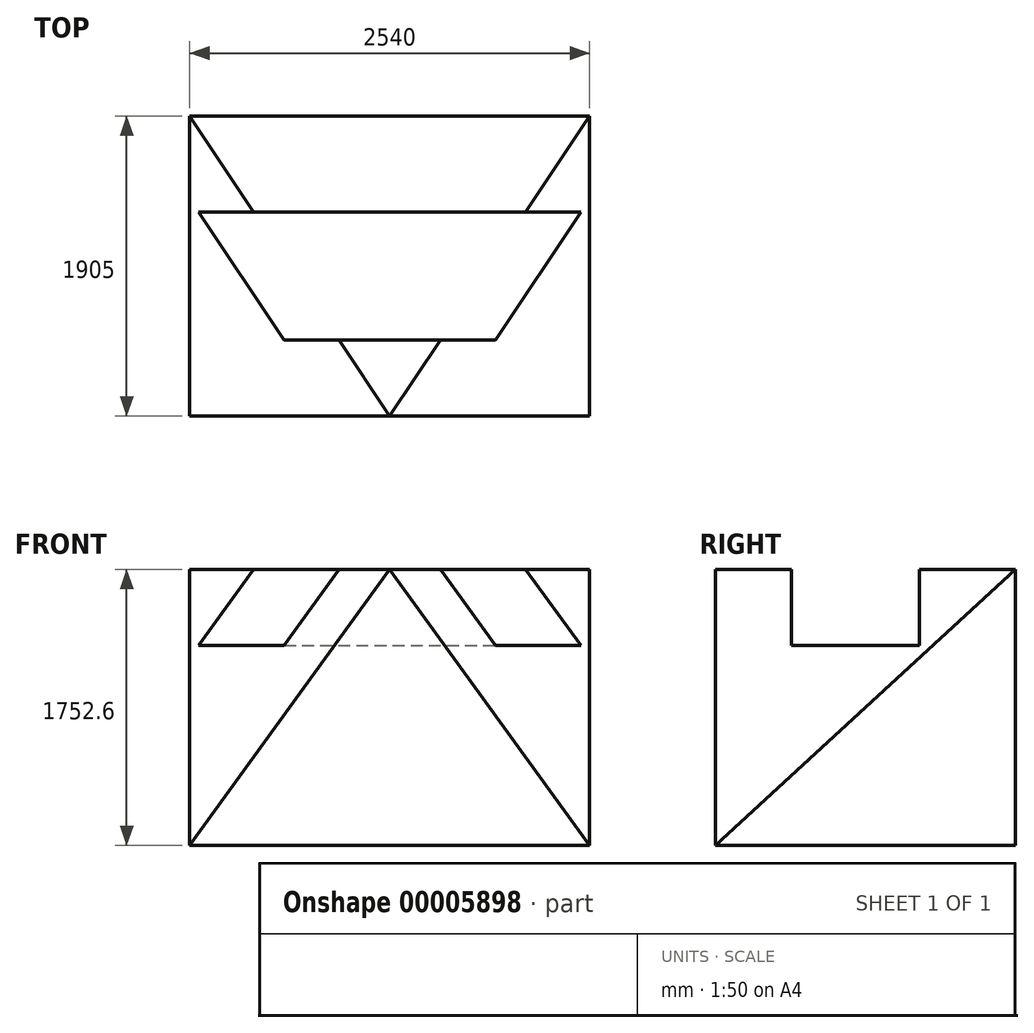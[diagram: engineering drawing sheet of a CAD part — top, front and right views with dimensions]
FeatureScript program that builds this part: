
annotation { "Feature Type Name" : "Feature", "Feature Type Description" : "" }
export const myFeature = defineFeature(function(context is Context, id is Id, definition is map)
    precondition{}
    {
        {
            var Q0;
            Q0=qCreatedBy(makeId("Front.planeOp"),FACE);
            var sketch = newSketch(context, id + "F0", { "sketchPlane" : qUnion([Q0])});
            skLineSegment(sketch, "E0", {"start": v(0, 0) * mm, "end": v(2540, 0) * mm});
            skLineSegment(sketch, "E1", {"start": v(2540, 0) * mm, "end": v(2540, -1752.6) * mm});
            skLineSegment(sketch, "E2", {"start": v(2540, -1752.6) * mm, "end": v(0, -1752.6) * mm});
            skLineSegment(sketch, "E3", {"start": v(0, -1752.6) * mm, "end": v(0, 0) * mm});
            skSolve(sketch);
        }
        {
            var Q0;
            Q0=makeQuery(id+"F0.imprint","IMPRINT",FACE,{"disambiguationData":[TD([[makeQuery(id+"F0.imprint","IMPRINT",EDGE,{"derivedFrom":sQuery(id+"F0.wireOp",EDGE,"E0")}),-1.0]])]});
            extrude(context, id + "F1", {"entities" : qUnion([Q0]), "depth" : 1905 * mm});
        }
        {
            var Q0;
            Q0=makeQuery(id+"F1.opExtrude","SWEPT_FACE",FACE,{"disambiguationData":[OSD([sQuery(id+"F0.wireOp",EDGE,"E1")])]});
            var sketch = newSketch(context, id + "F2", { "sketchPlane" : qUnion([Q0])});
            skLineSegment(sketch, "E4", {"start": v(0, 0) * mm, "end": v(-1905, -1752.6) * mm});
            skLineSegment(sketch, "E5", {"start": v(-1905, 0) * mm, "end": v(-1422.4, 0) * mm});
            skLineSegment(sketch, "E6", {"start": v(-1422.4, 0) * mm, "end": v(-1422.4, -482.6) * mm});
            skLineSegment(sketch, "E7", {"start": v(-1422.4, -482.6) * mm, "end": v(-609.6, -482.6) * mm});
            skLineSegment(sketch, "E8", {"start": v(-609.6, -482.6) * mm, "end": v(-609.6, 0) * mm});
            skLineSegment(sketch, "E9", {"start": v(-609.6, 0) * mm, "end": v(0, 0) * mm});
            skLineSegment(sketch, "E10", {"start": v(-1905, 0) * mm, "end": v(-1905, -1752.6) * mm});
            skSolve(sketch);
        }
        {
            var Q0;
            Q0=makeQuery(id+"F1.opExtrude","CAP_FACE",FACE,{"disambiguationData":[OSD([sQuery(id+"F0.wireOp",EDGE,"E0"),sQuery(id+"F0.wireOp",EDGE,"E1"),sQuery(id+"F0.wireOp",EDGE,"E2"),sQuery(id+"F0.wireOp",EDGE,"E3")])],"isStart":false});
            var sketch = newSketch(context, id + "F3", { "sketchPlane" : qUnion([Q0])});
            skLineSegment(sketch, "E11", {"start": v(1270, 0) * mm, "end": v(2540, -1752.6) * mm});
            skSolve(sketch);
        }
        {
            var Q0;
            Q0=sQuery(id+"F3.wireOp",VERTEX,"E11.start");
            var Q1;
            Q1=sQuery(id+"F2.wireOp",VERTEX,"E9.end");
            var Q2;
            Q2=sQuery(id+"F3.wireOp",VERTEX,"E11.end");
            cPlane(context, id + "F4", {"entities" : qUnion([Q0, Q1, Q2]), "cplaneType" : CPlaneType.THREE_POINT, "offset" : 152.4 * mm, "width" : 152.4 * mm, "height" : 152.4 * mm});
        }
        {
            var Q0;
            Q0=qCreatedBy(id+"F4.planeOp",FACE);
            var sketch = newSketch(context, id + "F5", { "sketchPlane" : qUnion([Q0])});
            skLineSegment(sketch, "E12", {"start": v(-3737.09, 250.38) * mm, "end": v(-2471.14, -4877.21) * mm});
            skLineSegment(sketch, "E13", {"start": v(-2471.14, -4877.21) * mm, "end": v(9797.3, -2905.45) * mm});
            skLineSegment(sketch, "E14", {"start": v(9797.3, -2905.45) * mm, "end": v(3353.72, 2692.03) * mm});
            skLineSegment(sketch, "E15", {"start": v(3353.72, 2692.03) * mm, "end": v(-3737.09, 250.38) * mm});
            skSolve(sketch);
        }
        {
            var Q0;
            Q0=makeQuery(id+"F5.imprint","IMPRINT",FACE,{"disambiguationData":[TD([[makeQuery(id+"F5.imprint","IMPRINT",EDGE,{"derivedFrom":sQuery(id+"F5.wireOp",EDGE,"E12")}),1.0]])]});
            extrude(context, id + "F6", {"entities" : qUnion([Q0]), "operationType" : NewBodyOperationType.REMOVE, "depth" : 2540 * mm});
        }
        {
            var Q0;
            Q0=makeQuery(id+"F1.opExtrude","CAP_VERTEX",VERTEX,{"disambiguationData":[OSD([sQuery(id+"F0.wireOp",EDGE,"E0"),sQuery(id+"F0.wireOp",EDGE,"E3")])],"isStart":true});
            var Q1;
            Q1=sQuery(id+"F3.wireOp",VERTEX,"E11.start");
            var Q2;
            Q2=makeQuery(id+"F1.opExtrude","CAP_VERTEX",VERTEX,{"disambiguationData":[OSD([sQuery(id+"F0.wireOp",EDGE,"E2"),sQuery(id+"F0.wireOp",EDGE,"E3")])],"isStart":false});
            cPlane(context, id + "F7", {"entities" : qUnion([Q0, Q1, Q2]), "cplaneType" : CPlaneType.THREE_POINT, "offset" : 152.4 * mm, "width" : 152.4 * mm, "height" : 152.4 * mm});
        }
        {
            var Q0;
            Q0=qCreatedBy(id+"F7.planeOp",FACE);
            var sketch = newSketch(context, id + "F8", { "sketchPlane" : qUnion([Q0])});
            skLineSegment(sketch, "E16", {"start": v(-1106.9, 0) * mm, "end": v(6334.9, 2345.3) * mm});
            skLineSegment(sketch, "E17", {"start": v(6334.9, 2345.3) * mm, "end": v(8031.7, -2892.8) * mm});
            skLineSegment(sketch, "E18", {"start": v(8031.7, -2892.8) * mm, "end": v(464.38, -2554.35) * mm});
            skLineSegment(sketch, "E19", {"start": v(464.38, -2554.35) * mm, "end": v(-1106.9, 0) * mm});
            skSolve(sketch);
        }
        {
            var Q0;
            Q0=makeQuery(id+"F8.imprint","IMPRINT",FACE,{"disambiguationData":[TD([[makeQuery(id+"F8.imprint","IMPRINT",EDGE,{"derivedFrom":sQuery(id+"F8.wireOp",EDGE,"E16")}),-1.0]])]});
            extrude(context, id + "F9", {"entities" : qUnion([Q0]), "operationType" : NewBodyOperationType.REMOVE, "depth" : 2540 * mm});
        }
        {
            var Q0;
            {var subQ2=sQuery(id+"F2.wireOp",EDGE,"E6");Q0=makeQuery(id+"F2.imprint","IMPRINT",FACE,{"disambiguationData":[TD([[makeQuery(id+"F2.imprint","IMPRINT",EDGE,{"derivedFrom":subQ2}),1.0]])]});}
            extrude(context, id + "F10", {"entities" : qUnion([Q0]), "operationType" : NewBodyOperationType.REMOVE, "oppositeDirection" : true, "depth" : 2540 * mm});
        }
    });
